# Revit family: Hatch-Floor-Best Access Doors-Flush_Aluminum-BA-AFL
name_source: partatom
category: Specialty Equipment
revit_build: Autodesk Revit 2017 (Build: 20160225_1515(x64)
units: mm (PartAtom-declared; Revit-internal decimal feet)

## family parameters
Cut with Voids When Loaded = No
Host = Face
OmniClass Number = 23.30.10.27.21
Part Type = Normal
Room Calculation Point = No
Round Connector Dimension = Use Diameter
Shared = No

## types (3) — shared parameters
Assembly Code = C1020700
Construction Material = Metal -  Best Access Doors - Aluminum
Default Elevation = 0"
Description = BA-AFL - Flush Aluminum Floor Hatch
Diamond Plate = Metal -  Best Access Doors - Aluminum Diamond Plate
Door Width = 24"
Finish = Metal -  Best Access Doors - Powder Coated White
Frame Depth = 1 3/4"
Manufacturer = Best Access Doors
Model = BA-AFL
Product data url = https://bimobject.com
URL = https://www.bestaccessdoors.com
Width Actual = 28"
Width Calc = 24"

## per-type parameters (varying)
| type | Door Height | Height Actual | Height Calc |
| Custom | 24" | 28 1/32" | 24" |
| 24x24 | 24" | 28 1/32" | 24" |
| 24x36 | 36" | 40 1/32" | 36" |

## geometry (parser evidence)
native form markers: Blend x4, Sweep x15
no freeform markers — native parametric forms only
